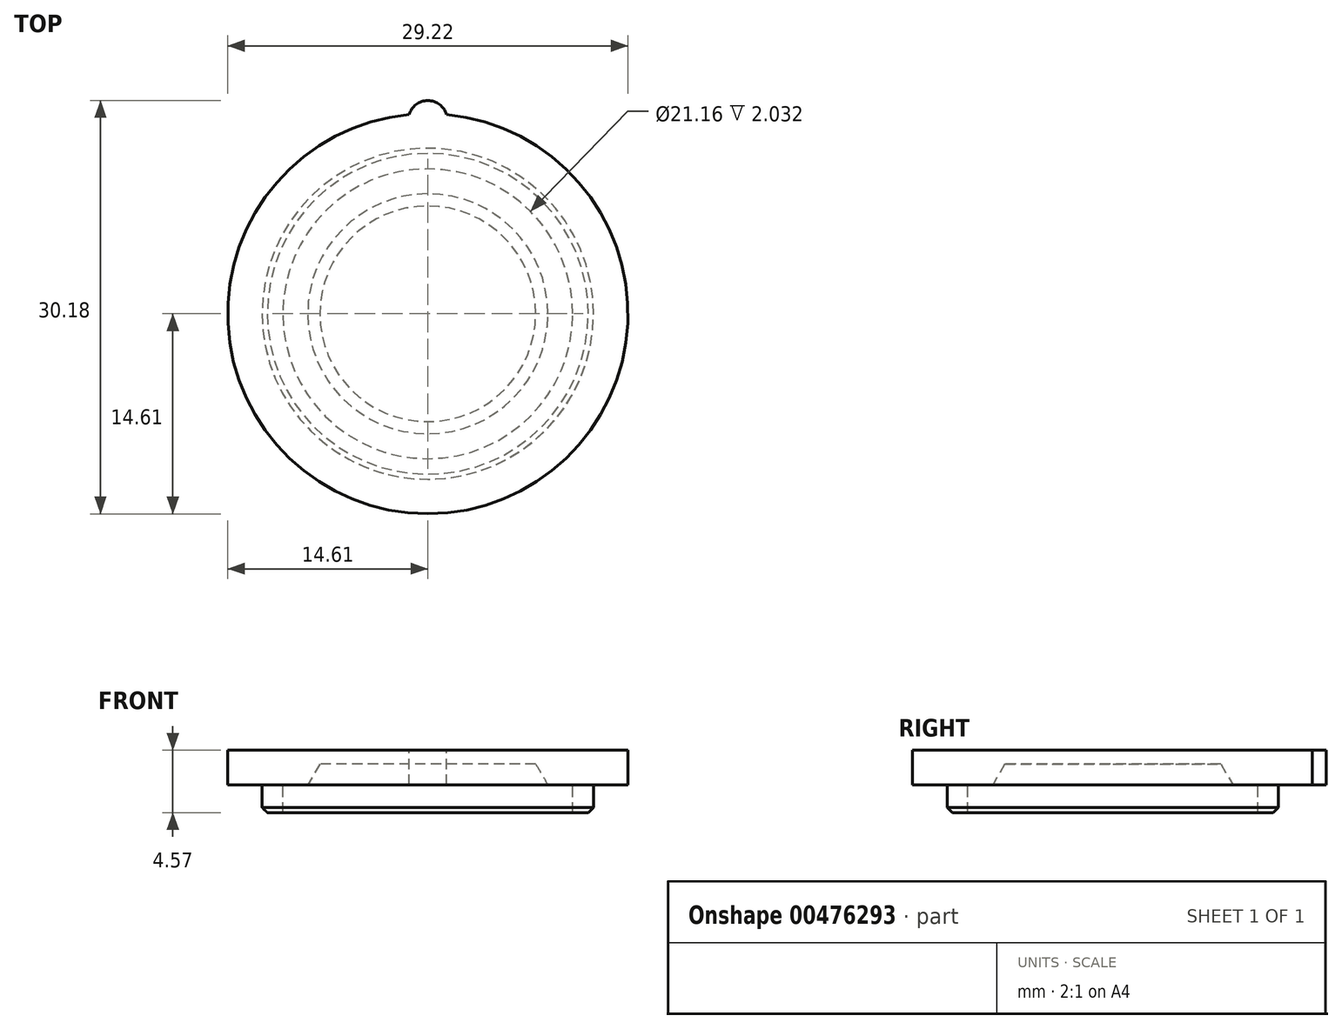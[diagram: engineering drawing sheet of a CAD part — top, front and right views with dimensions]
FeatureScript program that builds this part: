
annotation { "Feature Type Name" : "Feature", "Feature Type Description" : "" }
export const myFeature = defineFeature(function(context is Context, id is Id, definition is map)
    precondition{}
    {
        {
            var Q0;
            Q0=qCreatedBy(makeId("Top.planeOp"),FACE);
            var sketch = newSketch(context, id + "F0", { "sketchPlane" : qUnion([Q0])});
            skCircle(sketch, "E0", {"center": v(0, 0) * mm, "radius": 12.13 * mm});
            skSolve(sketch);
        }
        {
            var Q0;
            Q0=qCreatedBy(makeId("Front.planeOp"),FACE);
            var sketch = newSketch(context, id + "F1", { "sketchPlane" : qUnion([Q0])});
            skLineSegment(sketch, "E1.0", {"start": v(-12.1, 0) * mm, "end": v(-8.76, 0) * mm, "construction": true});
            skLineSegment(sketch, "E2", {"start": v(-12.1, 0) * mm, "end": v(-12.1, -2.03) * mm});
            skLineSegment(sketch, "E3", {"start": v(-12.1, -2.03) * mm, "end": v(-10.58, -2.03) * mm});
            skLineSegment(sketch, "E4", {"start": v(-10.58, -2.03) * mm, "end": v(-10.58, 0) * mm});
            skLineSegment(sketch, "E5", {"start": v(-10.58, 0) * mm, "end": v(-8.76, 0) * mm});
            skLineSegment(sketch, "E6", {"start": v(0, 1.52) * mm, "end": v(0, 2.54) * mm});
            skLineSegment(sketch, "E7", {"start": v(0, 2.54) * mm, "end": v(-14.6, 2.54) * mm});
            skLineSegment(sketch, "E8", {"start": v(-14.6, 2.54) * mm, "end": v(-14.6, 0) * mm});
            skLineSegment(sketch, "E9", {"start": v(-14.6, 0) * mm, "end": v(-12.1, 0) * mm});
            skLineSegment(sketch, "E10", {"start": v(0, 1.52) * mm, "end": v(0, 2.54) * mm, "construction": true});
            skLineSegment(sketch, "E11", {"start": v(0, 0) * mm, "end": v(0, -2.54) * mm, "construction": true});
            skLineSegment(sketch, "E12", {"start": v(-8.76, 0) * mm, "end": v(-7.87, 1.52) * mm});
            skLineSegment(sketch, "E13", {"start": v(-7.87, 1.52) * mm, "end": v(0, 1.52) * mm});
            skLineSegment(sketch, "E14.trimOffspring", {"start": v(0, 0) * mm, "end": v(12.13, 0) * mm, "construction": true});
            skSolve(sketch);
        }
        {
            var Q0;
            Q0 = qSketchRegion(id + "F1", true);
            var Q1;
            Q1=sQuery(id+"F1.wireOp",EDGE,"E11");
            revolve(context, id + "F2", {"entities" : qUnion([Q0]), "axis" : qUnion([Q1]), "revolveType" : RevolveType.FULL});
        }
        {
            var Q0;
            Q0=makeQuery(id+"F2.opRevolve","SWEPT_FACE",FACE,{"disambiguationData":[OSD([sQuery(id+"F1.wireOp",EDGE,"E7")])]});
            var sketch = newSketch(context, id + "F3", { "sketchPlane" : qUnion([Q0])});
            skCircle(sketch, "E15", {"center": v(0, 14.16) * mm, "radius": 1.4 * mm});
            skLineSegment(sketch, "E16", {"start": v(-1.36, 14.54) * mm, "end": v(1.36, 14.54) * mm, "construction": true});
            skSolve(sketch);
        }
        {
            var Q0;
            Q0 = qSketchRegion(id + "F3", true);
            var Q1;
            Q1=sQuery(id+"F3.wireOp",EDGE,"E15");
            var Q2;
            Q2=makeQuery(id+"F2.opRevolve","SWEPT_FACE",FACE,{"disambiguationData":[OSD([sQuery(id+"F1.wireOp",EDGE,"E9")])]});
            extrude(context, id + "F4", {"entities" : qUnion([Q0]), "operationType" : NewBodyOperationType.ADD, "surfaceEntities" : qUnion([Q1]), "endBound" : BoundingType.UP_TO_SURFACE, "oppositeDirection" : true, "endBoundEntityFace" : qUnion([Q2]), "depth" : 25.4 * mm});
        }
        {
            var Q0;
            Q0=makeQuery(id+"F2.opRevolve","SWEPT_EDGE",EDGE,{"disambiguationData":[OSD([sQuery(id+"F1.wireOp",EDGE,"E2"),sQuery(id+"F1.wireOp",EDGE,"E3")])]});
            chamfer(context, id + "F5", {"entities" : qUnion([Q0]), "width" : 0.38 * mm, "tangentPropagation" : true});
        }
    });
